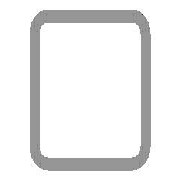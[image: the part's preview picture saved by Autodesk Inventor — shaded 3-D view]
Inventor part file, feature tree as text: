
AUTODESK INVENTOR PART (.ipt)
format: ipt  version: 2025 (Build 290162010, 162A)  size: 134,144 bytes
history: native  units: mm (DEFAULTED — no unit token found)
features: other x4, sketch x1, plane x1
ambient origin geometry x8: Origin, YZ Plane, XZ Plane, XY Plane, X Axis, Y Axis, Z Axis, Center Point
bodies: Solid1 (feature_tree), Body (feature_tree)
feature tree (6):
  parser-record x1  (decoder bookkeeping rows leaked as tree rows — omitted from the tree; the rows remain in map.json)
  other  "Driven Length"
  other  "Start Plane"
  other  "End Plane"
  sketch  "Sketch3"  dims[d3=2150.0mm d4=0.0mm d7=8.0mm d9=50.0mm d11=50.0mm d12=4.0mm d13=-0.0mm d14=2150.0mm d15=25.0mm d16=25.0mm d17=90.0deg d18=2150.0mm]
  plane  "Work Plane3"
